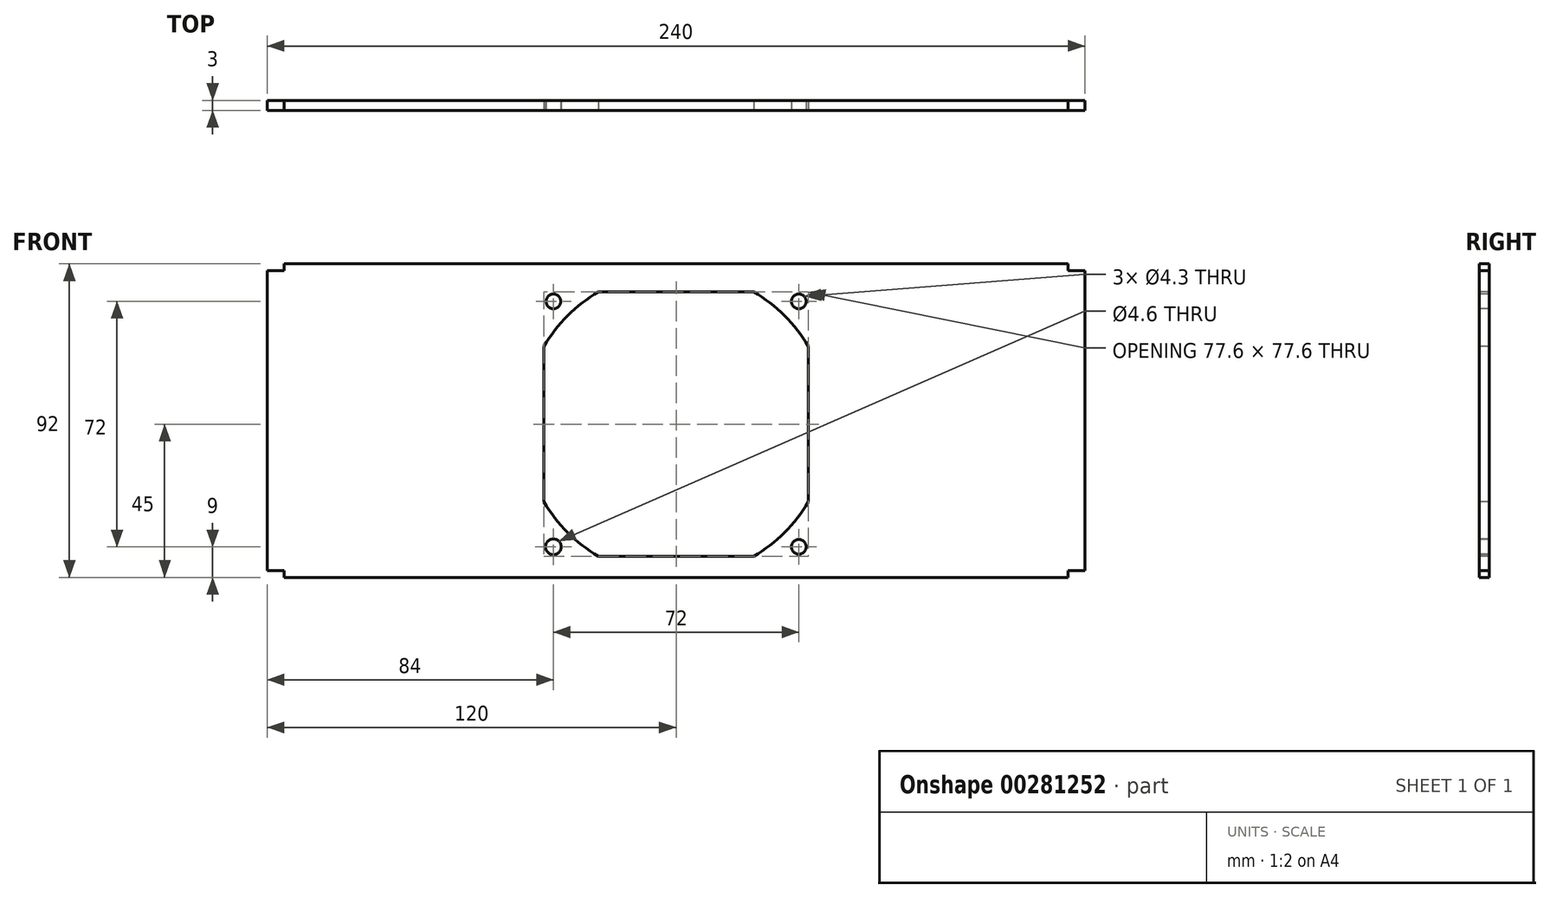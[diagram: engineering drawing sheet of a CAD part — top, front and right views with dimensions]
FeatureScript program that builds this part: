
annotation { "Feature Type Name" : "Feature", "Feature Type Description" : "" }
export const myFeature = defineFeature(function(context is Context, id is Id, definition is map)
    precondition{}
    {
        {
            var Q0;
            Q0=qCreatedBy(makeId("Front.planeOp"),FACE);
            var sketch = newSketch(context, id + "F0", { "sketchPlane" : qUnion([Q0])});
            skLineSegment(sketch, "E0.bottom", {"start": v(120, -47) * mm, "end": v(-120, -47) * mm});
            skLineSegment(sketch, "E0.top", {"start": v(120, 47) * mm, "end": v(-120, 47) * mm});
            skLineSegment(sketch, "E0.left", {"start": v(120, -47) * mm, "end": v(120, 47) * mm});
            skLineSegment(sketch, "E0.right", {"start": v(-120, -47) * mm, "end": v(-120, 47) * mm});
            skPoint(sketch, "E0.middle", {"position": v(0, 0) * mm});
            skSolve(sketch);
        }
        {
            var Q0;
            Q0=qSketchRegion(id+"F0",true);
            extrude(context, id + "F1", {"entities" : qUnion([Q0]), "depth" : 3 * mm});
        }
        {
            var Q0;
            Q0=makeQuery(id+"F1.opExtrude","CAP_FACE",FACE,{"disambiguationData":[OSD([sQuery(id+"F0.wireOp",EDGE,"E0.bottom"),sQuery(id+"F0.wireOp",EDGE,"E0.top"),sQuery(id+"F0.wireOp",EDGE,"E0.left"),sQuery(id+"F0.wireOp",EDGE,"E0.right")])],"isStart":false});
            var sketch = newSketch(context, id + "F2", { "sketchPlane" : qUnion([Q0])});
            skLineSegment(sketch, "E1.bottom", {"start": v(-120, 47) * mm, "end": v(-115, 47) * mm});
            skLineSegment(sketch, "E1.top", {"start": v(-120, 45) * mm, "end": v(-115, 45) * mm});
            skLineSegment(sketch, "E1.left", {"start": v(-120, 47) * mm, "end": v(-120, 45) * mm});
            skLineSegment(sketch, "E1.right", {"start": v(-115, 47) * mm, "end": v(-115, 45) * mm});
            skLineSegment(sketch, "E2.bottom", {"start": v(-120, -47) * mm, "end": v(-115, -47) * mm});
            skLineSegment(sketch, "E2.top", {"start": v(-120, -43) * mm, "end": v(-115, -43) * mm});
            skLineSegment(sketch, "E2.left", {"start": v(-120, -47) * mm, "end": v(-120, -43) * mm});
            skLineSegment(sketch, "E2.right", {"start": v(-115, -47) * mm, "end": v(-115, -43) * mm});
            skLineSegment(sketch, "E3.bottom", {"start": v(120, -47) * mm, "end": v(115, -47) * mm});
            skLineSegment(sketch, "E3.top", {"start": v(120, -43) * mm, "end": v(115, -43) * mm});
            skLineSegment(sketch, "E3.left", {"start": v(120, -47) * mm, "end": v(120, -43) * mm});
            skLineSegment(sketch, "E3.right", {"start": v(115, -47) * mm, "end": v(115, -43) * mm});
            skLineSegment(sketch, "E4.bottom", {"start": v(120, 47) * mm, "end": v(115, 47) * mm});
            skLineSegment(sketch, "E4.top", {"start": v(120, 45) * mm, "end": v(115, 45) * mm});
            skLineSegment(sketch, "E4.left", {"start": v(120, 47) * mm, "end": v(120, 45) * mm});
            skLineSegment(sketch, "E4.right", {"start": v(115, 47) * mm, "end": v(115, 45) * mm});
            skLineSegment(sketch, "E5.bottom", {"start": v(115, -47) * mm, "end": v(-115, -47) * mm});
            skLineSegment(sketch, "E5.top", {"start": v(115, -45) * mm, "end": v(-115, -45) * mm});
            skLineSegment(sketch, "E5.left", {"start": v(115, -47) * mm, "end": v(115, -45) * mm});
            skLineSegment(sketch, "E5.right", {"start": v(-115, -47) * mm, "end": v(-115, -45) * mm});
            skSolve(sketch);
        }
        {
            var Q0;
            Q0 = qSketchRegion(id + "F2", true);
            extrude(context, id + "F3", {"entities" : qUnion([Q0]), "operationType" : NewBodyOperationType.REMOVE, "oppositeDirection" : true, "depth" : 25 * mm});
        }
        {
            var Q0;
            Q0=makeQuery(id+"F1.opExtrude","CAP_FACE",FACE,{"disambiguationData":[OSD([sQuery(id+"F0.wireOp",EDGE,"E0.bottom"),sQuery(id+"F0.wireOp",EDGE,"E0.top"),sQuery(id+"F0.wireOp",EDGE,"E0.left"),sQuery(id+"F0.wireOp",EDGE,"E0.right")])],"isStart":false});
            var sketch = newSketch(context, id + "F4", { "sketchPlane" : qUnion([Q0])});
            skLineSegment(sketch, "E6.bottom", {"start": v(40, -40) * mm, "end": v(-40, -40) * mm});
            skLineSegment(sketch, "E6.top", {"start": v(40, 40) * mm, "end": v(-40, 40) * mm});
            skLineSegment(sketch, "E6.left", {"start": v(40, -40) * mm, "end": v(40, 40) * mm});
            skLineSegment(sketch, "E6.right", {"start": v(-40, -40) * mm, "end": v(-40, 40) * mm});
            skPoint(sketch, "E6.middle", {"position": v(0, 0) * mm});
            skLineSegment(sketch, "E7.bottom", {"start": v(36, -36) * mm, "end": v(27, -36) * mm});
            skLineSegment(sketch, "E7.top", {"start": v(36, 36) * mm, "end": v(27, 36) * mm});
            skLineSegment(sketch, "E7.left", {"start": v(36, -36) * mm, "end": v(36, -27) * mm});
            skLineSegment(sketch, "E7.right", {"start": v(-36, -36) * mm, "end": v(-36, -27) * mm});
            skCircle(sketch, "E8", {"center": v(-36, 36) * mm, "radius": 2.15 * mm});
            skCircle(sketch, "E9", {"center": v(36, 36) * mm, "radius": 2.15 * mm});
            skCircle(sketch, "E10", {"center": v(36, -36) * mm, "radius": 2.15 * mm});
            skCircle(sketch, "E11", {"center": v(-36, -36) * mm, "radius": 2.3 * mm});
            skArc(sketch, "E12", {"start": v(22.8, -38.8) * mm, "mid": v(31.82, -31.82) * mm, "end": v(38.8, -22.8) * mm});
            skArc(sketch, "E13.trimOffspring", {"start": v(-38.8, -22.8) * mm, "mid": v(-31.82, -31.82) * mm, "end": v(-22.8, -38.8) * mm});
            skArc(sketch, "E14.trimOffspring", {"start": v(-22.8, 38.8) * mm, "mid": v(-31.82, 31.82) * mm, "end": v(-38.8, 22.8) * mm});
            skArc(sketch, "E15.trimOffspring", {"start": v(38.8, 22.8) * mm, "mid": v(31.82, 31.82) * mm, "end": v(22.8, 38.8) * mm});
            skLineSegment(sketch, "E16.bottom", {"start": v(38.8, -38.8) * mm, "end": v(-38.8, -38.8) * mm});
            skLineSegment(sketch, "E16.top", {"start": v(38.8, 38.8) * mm, "end": v(-38.8, 38.8) * mm});
            skLineSegment(sketch, "E16.left", {"start": v(38.8, -38.8) * mm, "end": v(38.8, 38.8) * mm});
            skLineSegment(sketch, "E16.right", {"start": v(-38.8, -38.8) * mm, "end": v(-38.8, 38.8) * mm});
            skLineSegment(sketch, "E17.trimOffspring", {"start": v(-36, 27) * mm, "end": v(-36, 36) * mm});
            skLineSegment(sketch, "E18.trimOffspring", {"start": v(36, 27) * mm, "end": v(36, 36) * mm});
            skLineSegment(sketch, "E19.trimOffspring", {"start": v(-27, 36) * mm, "end": v(-36, 36) * mm});
            skLineSegment(sketch, "E20.trimOffspring", {"start": v(-27, -36) * mm, "end": v(-36, -36) * mm});
            skSolve(sketch);
        }
        {
            var Q0;
            {var subQ0=sQuery(id+"F4.wireOp",EDGE,"E17.trimOffspring");var subQ1=sQuery(id+"F4.wireOp",EDGE,"E8");var subQ2=makeQuery(id+"F4.imprint","INTERSECT",VERTEX,{"derivedFrom":[subQ1,subQ0]});Q0=makeQuery(id+"F4.imprint","IMPRINT",FACE,{"disambiguationData":[TD([[makeQuery(id+"F4.imprint","IMPRINT",EDGE,{"disambiguationData":[TD([[subQ2,1.0]])],"derivedFrom":subQ1}),1.0]])]});}
            var Q1;
            {var subQ0=sQuery(id+"F4.wireOp",EDGE,"E17.trimOffspring");var subQ1=sQuery(id+"F4.wireOp",EDGE,"E8");var subQ2=makeQuery(id+"F4.imprint","INTERSECT",VERTEX,{"derivedFrom":[subQ1,subQ0]});Q1=makeQuery(id+"F4.imprint","IMPRINT",FACE,{"disambiguationData":[TD([[makeQuery(id+"F4.imprint","IMPRINT",EDGE,{"disambiguationData":[TD([[subQ2,-1.0]])],"derivedFrom":subQ1}),1.0]])]});}
            var Q2;
            {var subQ0=sQuery(id+"F4.wireOp",EDGE,"E18.trimOffspring");var subQ1=sQuery(id+"F4.wireOp",EDGE,"E7.top");var subQ2=makeQuery(id+"F4.imprint","INTERSECT",VERTEX,{"derivedFrom":[subQ1,subQ0]});Q2=makeQuery(id+"F4.imprint","IMPRINT",FACE,{"disambiguationData":[TD([[makeQuery(id+"F4.imprint","IMPRINT",EDGE,{"disambiguationData":[TD([[subQ2,-1.0]])],"derivedFrom":subQ1}),-1.0]])]});}
            var Q3;
            {var subQ0=sQuery(id+"F4.wireOp",EDGE,"E18.trimOffspring");var subQ1=sQuery(id+"F4.wireOp",EDGE,"E7.top");var subQ2=makeQuery(id+"F4.imprint","INTERSECT",VERTEX,{"derivedFrom":[subQ1,subQ0]});Q3=makeQuery(id+"F4.imprint","IMPRINT",FACE,{"disambiguationData":[TD([[makeQuery(id+"F4.imprint","IMPRINT",EDGE,{"disambiguationData":[TD([[subQ2,-1.0]])],"derivedFrom":subQ1}),1.0]])]});}
            var Q4;
            {var subQ0=sQuery(id+"F4.wireOp",EDGE,"E7.left");var subQ1=sQuery(id+"F4.wireOp",EDGE,"E7.bottom");var subQ2=makeQuery(id+"F4.imprint","INTERSECT",VERTEX,{"derivedFrom":[subQ1,subQ0]});Q4=makeQuery(id+"F4.imprint","IMPRINT",FACE,{"disambiguationData":[TD([[makeQuery(id+"F4.imprint","IMPRINT",EDGE,{"disambiguationData":[TD([[subQ2,-1.0]])],"derivedFrom":subQ1}),1.0]])]});}
            var Q5;
            {var subQ0=sQuery(id+"F4.wireOp",EDGE,"E7.left");var subQ1=sQuery(id+"F4.wireOp",EDGE,"E7.bottom");var subQ2=makeQuery(id+"F4.imprint","INTERSECT",VERTEX,{"derivedFrom":[subQ1,subQ0]});Q5=makeQuery(id+"F4.imprint","IMPRINT",FACE,{"disambiguationData":[TD([[makeQuery(id+"F4.imprint","IMPRINT",EDGE,{"disambiguationData":[TD([[subQ2,-1.0]])],"derivedFrom":subQ1}),-1.0]])]});}
            var Q6;
            {var subQ0=sQuery(id+"F4.wireOp",EDGE,"E20.trimOffspring");var subQ1=sQuery(id+"F4.wireOp",EDGE,"E7.right");var subQ2=makeQuery(id+"F4.imprint","INTERSECT",VERTEX,{"derivedFrom":[subQ1,subQ0]});Q6=makeQuery(id+"F4.imprint","IMPRINT",FACE,{"disambiguationData":[TD([[makeQuery(id+"F4.imprint","IMPRINT",EDGE,{"disambiguationData":[TD([[subQ2,-1.0]])],"derivedFrom":subQ1}),1.0]])]});}
            var Q7;
            {var subQ0=sQuery(id+"F4.wireOp",EDGE,"E20.trimOffspring");var subQ1=sQuery(id+"F4.wireOp",EDGE,"E7.right");var subQ2=makeQuery(id+"F4.imprint","INTERSECT",VERTEX,{"derivedFrom":[subQ1,subQ0]});Q7=makeQuery(id+"F4.imprint","IMPRINT",FACE,{"disambiguationData":[TD([[makeQuery(id+"F4.imprint","IMPRINT",EDGE,{"disambiguationData":[TD([[subQ2,-1.0]])],"derivedFrom":subQ1}),-1.0]])]});}
            var Q8;
            {var subQ16=sQuery(id+"F4.wireOp",EDGE,"E12");var subQ17=makeQuery(id+"F4.imprint","INTERSECT",VERTEX,{"derivedFrom":[sQuery(id+"F4.wireOp",EDGE,"E7.bottom"),subQ16]});Q8=makeQuery(id+"F4.imprint","IMPRINT",FACE,{"disambiguationData":[TD([[makeQuery(id+"F4.imprint","IMPRINT",EDGE,{"disambiguationData":[TD([[subQ17,1.0]])],"derivedFrom":subQ16}),1.0]])]});}
            extrude(context, id + "F5", {"entities" : qUnion([Q0, Q1, Q2, Q3, Q4, Q5, Q6, Q7, Q8]), "operationType" : NewBodyOperationType.REMOVE, "oppositeDirection" : true, "depth" : 25 * mm});
        }
    });
